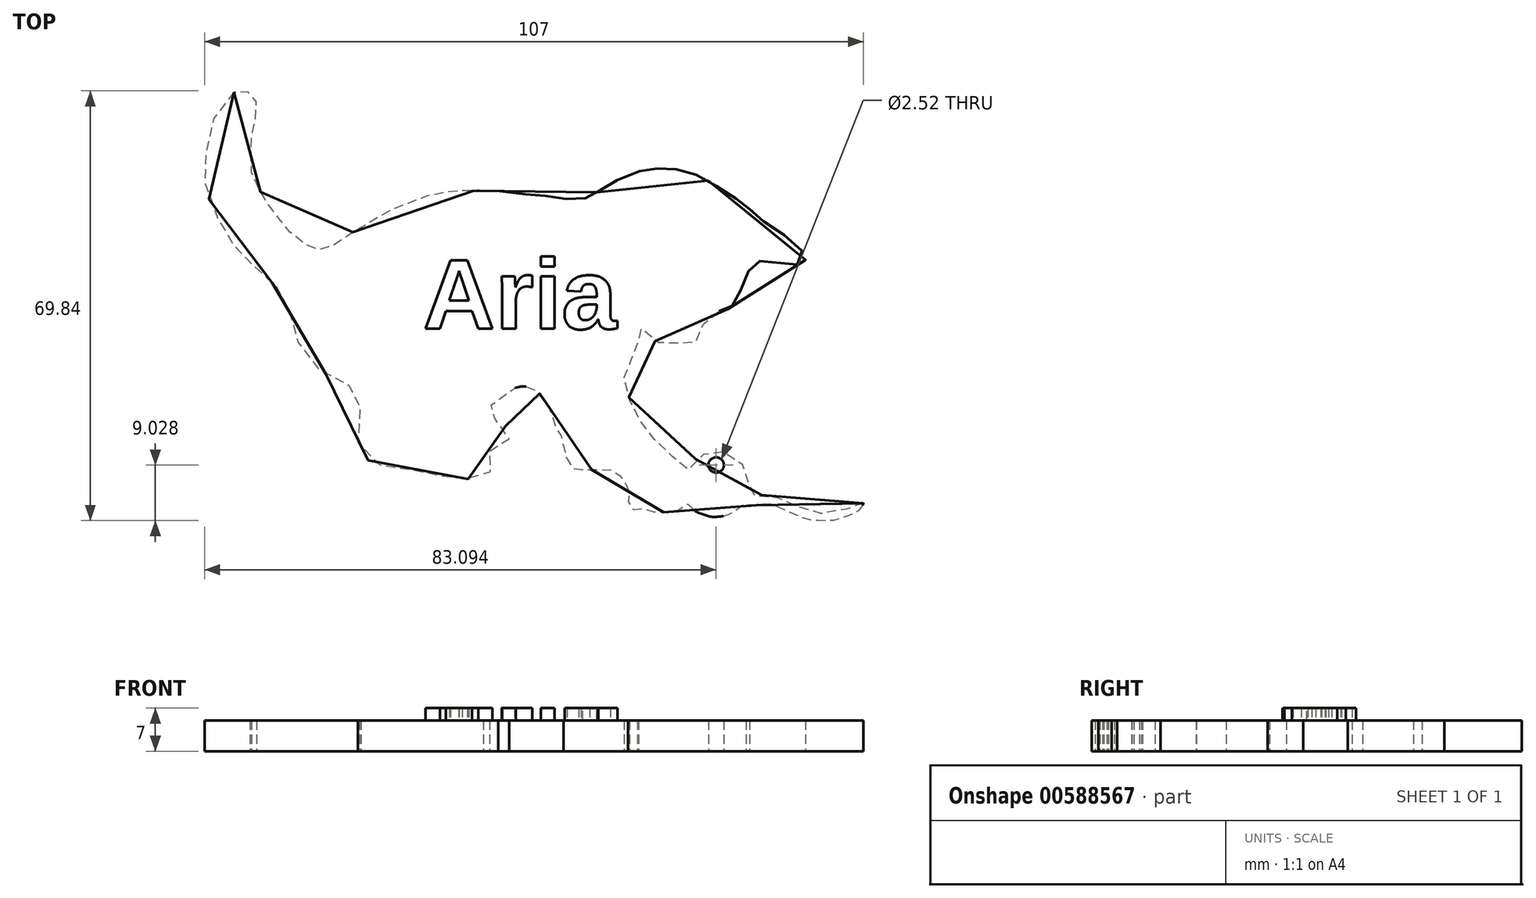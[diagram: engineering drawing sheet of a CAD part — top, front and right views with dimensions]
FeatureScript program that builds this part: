
annotation { "Feature Type Name" : "Feature", "Feature Type Description" : "" }
export const myFeature = defineFeature(function(context is Context, id is Id, definition is map)
    precondition{}
    {
        {
            var Q0;
            Q0=qCreatedBy(makeId("Top.planeOp"),FACE);
            var sketch = newSketch(context, id + "F0", { "sketchPlane" : qUnion([Q0])});
            skFitSpline(sketch, "E0", {"points": [v(-50.05, 29.56) * mm, v(-51.28, 28.57) * mm, v(-52.27, 27.19) * mm, v(-53.3, 25.4) * mm, v(-53.8, 23.53) * mm, v(-54.35, 21.95) * mm, v(-54.64, 19.63) * mm, v(-54.74, 17.95) * mm, v(-54.8, 16.76) * mm, v(-54.84, 15.43) * mm, v(-54.4, 13.06) * mm, v(-53.65, 10.84) * mm, v(-52.76, 9.16) * mm, v(-52.07, 7.77) * mm, v(-51.18, 6.34) * mm, v(-50.4, 5.1) * mm, v(-49.65, 4.17) * mm, v(-48.91, 3.57) * mm, v(-47.97, 2.44) * mm, v(-46.79, 1.25) * mm, v(-45.65, 0) * mm, v(-44.61, -0.82) * mm, v(-43.48, -1.76) * mm, v(-42.44, -2.6) * mm, v(-41.85, -3.04) * mm, v(-41.4, -4.38) * mm, v(-41.06, -6.1) * mm, v(-40.61, -8.33) * mm, v(-40.27, -9.56) * mm, v(-39.63, -11.15) * mm, v(-38.74, -12.92) * mm, v(-37.5, -14.4) * mm, v(-36.27, -15.5) * mm, v(-34.69, -16.48) * mm, v(-32.86, -17.27) * mm, v(-31.23, -18.2) * mm, v(-30.14, -19) * mm, v(-29.5, -19.6) * mm, v(-29.6, -20.83) * mm, v(-29.6, -22.3) * mm, v(-29.8, -24.24) * mm, v(-29.9, -26.3) * mm, v(-29.85, -28.04) * mm, v(-29, -29.42) * mm, v(-27.87, -30.6) * mm, v(-25.7, -31.15) * mm, v(-23.77, -31.64) * mm, v(-21.15, -31.84) * mm, v(-19.67, -32.04) * mm, v(-18.04, -32) * mm, v(-17.4, -32.14) * mm, v(-16.76, -32.58) * mm, v(-15.82, -33.08) * mm, v(-14.48, -33.57) * mm, v(-13.45, -33.42) * mm, v(-12.85, -33.23) * mm, v(-11.77, -33.37) * mm, v(-10.93, -33.52) * mm, v(-9.7, -32.93) * mm, v(-8.6, -32.19) * mm, v(-7.72, -32.04) * mm, v(-7.17, -30.9) * mm, v(-7.86, -29.42) * mm, v(-8.56, -28.78) * mm, v(-8.5, -28.58) * mm, v(-7.77, -28.48) * mm, v(-6.23, -28.04) * mm, v(-5.5, -27.25) * mm, v(-5.44, -25.82) * mm, v(-5.79, -24.88) * mm, v(-6.68, -24.19) * mm, v(-7.62, -23.54) * mm, v(-8.36, -23.1) * mm, v(-9.5, -23.1) * mm, v(-9.5, -22.8) * mm, v(-8.85, -21.96) * mm, v(-7.72, -20.68) * mm, v(-6.58, -19.79) * mm, v(-5.25, -18.8) * mm, v(-4.4, -18.5) * mm, v(-3.07, -18.26) * mm, v(-1.89, -18.5) * mm, v(-0.6, -19.25) * mm, v(0, -20.28) * mm, v(0.78, -21.32) * mm, v(1.57, -22.65) * mm, v(1.87, -24.09) * mm, v(2.26, -25.12) * mm, v(2.7, -25.96) * mm, v(3.4, -26.75) * mm, v(3.45, -28.33) * mm, v(3.94, -30.01) * mm, v(4.98, -31.6) * mm, v(6.6, -31.84) * mm, v(8.14, -31.8) * mm, v(10.66, -31.84) * mm, v(11.85, -32) * mm, v(12.83, -33.13) * mm, v(13.48, -34.06) * mm, v(14.12, -34.7) * mm, v(13.97, -36.04) * mm, v(13.97, -37.08) * mm, v(14.36, -38.02) * mm, v(15.45, -38.31) * mm, v(16.49, -38.12) * mm, v(17.82, -38.56) * mm, v(19.55, -38.7) * mm, v(21.13, -38.51) * mm, v(22.71, -38.12) * mm, v(23.85, -37.37) * mm, v(24.64, -38.31) * mm, v(26.02, -39.05) * mm, v(27.4, -39.45) * mm, v(29.33, -39.35) * mm, v(30.71, -38.9) * mm, v(31.85, -38.02) * mm, v(32.57, -37.58) * mm, v(33.82, -37.44) * mm, v(34.8, -37.58) * mm, v(36.16, -37.34) * mm, v(37.54, -37.52) * mm, v(39.33, -38.33) * mm, v(40.9, -39) * mm, v(42.8, -39.78) * mm, v(45.07, -40) * mm, v(47.44, -39.99) * mm, v(49.68, -39.25) * mm, v(50.8, -38.8) * mm, v(51.96, -37.84) * mm, v(52.05, -36.83) * mm, v(51.16, -37.42) * mm, v(49.53, -38.16) * mm, v(47.36, -38.86) * mm, v(45.43, -38.96) * mm, v(43.8, -38.56) * mm, v(42.12, -38.07) * mm, v(40.4, -37.23) * mm, v(39.11, -36.63) * mm, v(37.83, -36.29) * mm, v(36.1, -36) * mm, v(34.91, -36) * mm, v(33.13, -36.34) * mm, v(33.53, -35.25) * mm, v(33.63, -33.97) * mm, v(33.33, -32.68) * mm, v(32.6, -31.1) * mm, v(31.65, -30.16) * mm, v(30.17, -29.13) * mm, v(28.56, -28.9) * mm, v(27.4, -28.98) * mm, v(26.27, -29.32) * mm, v(24.98, -30.06) * mm, v(23.8, -31.5) * mm, v(23.65, -31.8) * mm, v(22.76, -31.05) * mm, v(21.63, -30.11) * mm, v(20.54, -29.08) * mm, v(19.16, -27.84) * mm, v(17.82, -26.4) * mm, v(17.08, -25.37) * mm, v(15.94, -23.89) * mm, v(15.2, -22.36) * mm, v(14.36, -20.88) * mm, v(13.82, -19.05) * mm, v(13.43, -17.52) * mm, v(13.33, -16.23) * mm, v(13.62, -15.2) * mm, v(14.22, -14.26) * mm, v(15.15, -13.07) * mm, v(15.6, -11.79) * mm, v(15.6, -11.1) * mm, v(15.45, -9.37) * mm, v(15.6, -8.43) * mm, v(16.49, -9.22) * mm, v(17.38, -10.3) * mm, v(18.71, -11.05) * mm, v(19.95, -11.3) * mm, v(21.77, -11.24) * mm, v(22.51, -11.2) * mm, v(23.2, -11.34) * mm, v(24.4, -11.44) * mm, v(25.03, -10.85) * mm, v(25.68, -9.56) * mm, v(26.02, -8.58) * mm, v(26.32, -7.84) * mm, v(27.16, -6.95) * mm, v(28.44, -6.2) * mm, v(29.33, -5.76) * mm, v(30.07, -5.71) * mm, v(31.01, -4.97) * mm, v(31.8, -3.64) * mm, v(32.44, -2.1) * mm, v(33.28, 0) * mm, v(33.73, 0.9) * mm, v(34.62, 1.8) * mm, v(35.7, 2.2) * mm, v(36.94, 1.94) * mm, v(38.67, 1.85) * mm, v(40.35, 1.6) * mm, v(42.62, 1.9) * mm, v(42.42, 3.43) * mm, v(40.7, 5.25) * mm, v(38.27, 7.03) * mm, v(35.9, 8.56) * mm, v(34.52, 9.8) * mm, v(33.58, 10.59) * mm, v(32.64, 11.43) * mm, v(31.36, 12.37) * mm, v(29.28, 13.65) * mm, v(26.86, 15.23) * mm, v(24.84, 16.22) * mm, v(22.86, 16.76) * mm, v(20.98, 17.1) * mm, v(19.3, 17.16) * mm, v(17.67, 17.16) * mm, v(16.2, 16.86) * mm, v(14.66, 16.32) * mm, v(11.65, 14.99) * mm, v(10.17, 14.05) * mm, v(9.08, 13.4) * mm, v(7.8, 12.52) * mm, v(6.6, 12.27) * mm, v(4.68, 12.22) * mm, v(3, 12.27) * mm, v(0.73, 12.66) * mm, v(-0.9, 12.86) * mm, v(-2.97, 12.96) * mm, v(-6.09, 13.36) * mm, v(-9.2, 13.6) * mm, v(-11.42, 13.55) * mm, v(-13.35, 13.5) * mm, v(-15.17, 13.36) * mm, v(-17.8, 12.91) * mm, v(-20.31, 12.12) * mm, v(-22.04, 11.38) * mm, v(-24.51, 10.44) * mm, v(-26.49, 9.3) * mm, v(-28.86, 7.87) * mm, v(-30.64, 6.88) * mm, v(-32.31, 5.7) * mm, v(-33.9, 4.71) * mm, v(-35.67, 4.02) * mm, v(-36.86, 4.02) * mm, v(-38.44, 4.8) * mm, v(-40.32, 6.24) * mm, v(-42.14, 8.07) * mm, v(-43.18, 9.65) * mm, v(-44.86, 11.77) * mm, v(-45.8, 13.45) * mm, v(-46.69, 15.13) * mm, v(-47.48, 17.9) * mm, v(-47.23, 19.73) * mm, v(-47.23, 21.95) * mm, v(-46.74, 24.37) * mm, v(-46.44, 26.89) * mm, v(-46.54, 28.47) * mm, v(-47.33, 29.36) * mm, v(-48.62, 29.75) * mm, v(-50.05, 29.56) * mm]});
            skSolve(sketch);
        }
        {
            var Q0;
            Q0 = qSketchRegion(id + "F2", true);
            var Q1;
            Q1=makeQuery(id+"F0.imprint","IMPRINT",FACE,{"disambiguationData":[TD([[makeQuery(id+"F0.imprint","IMPRINT",EDGE,{"derivedFrom":sQuery(id+"F0.wireOp",EDGE,"E0")}),1.0]])]});
            extrude(context, id + "F1", {"entities" : qUnion([Q0, Q1]), "depth" : 5 * mm, "offsetDistance" : 25 * mm});
        }
        {
            var Q0;
            Q0=makeQuery(id+"F1.opExtrude","CAP_FACE",FACE,{"disambiguationData":[OSD([sQuery(id+"F0.wireOp",EDGE,"E0")])],"isStart":false});
            var sketch = newSketch(context, id + "F2", { "sketchPlane" : qUnion([Q0])});
            skText(sketch, "E1", { "text": "Aria", "fontName": "Arimo-Bold.ttf"});
            const initialGuessF2  = {"E1": [-0.01936, -0.0089, 1, 0, 0.01166]};
            skSetInitialGuess(sketch, initialGuessF2);
            skSolve(sketch);
        }
        {
            var Q0;
            Q0 = qSketchRegion(id + "F2", true);
            var Q1;
            Q1 = qSketchRegion(id + "F4", true);
            extrude(context, id + "F3", {"entities" : qUnion([Q0, Q1]), "operationType" : NewBodyOperationType.ADD, "depth" : 2 * mm, "offsetDistance" : 25 * mm});
        }
        {
            var Q0;
            Q0=qCreatedBy(makeId("Front.planeOp"),FACE);
            var sketch = newSketch(context, id + "F4", { "sketchPlane" : qUnion([Q0])});
            skSolve(sketch);
        }
        {
            var Q0;
            Q0=qCreatedBy(makeId("Top.planeOp"),FACE);
            var sketch = newSketch(context, id + "F5", { "sketchPlane" : qUnion([Q0])});
            skCircle(sketch, "E2", {"center": v(28.72, -33.28) * mm, "radius": 1.26 * mm});
            skSolve(sketch);
        }
        {
            var Q0;
            Q0=makeQuery(id+"F5.imprint","IMPRINT",FACE,{"disambiguationData":[TD([[makeQuery(id+"F5.imprint","IMPRINT",EDGE,{"derivedFrom":sQuery(id+"F5.wireOp",EDGE,"E2")}),1.0]])]});
            extrude(context, id + "F6", {"entities" : qUnion([Q0]), "operationType" : NewBodyOperationType.ADD, "depth" : 5 * mm, "offsetDistance" : 25 * mm});
        }
        {
            var Q0;
            Q0=qCreatedBy(makeId("Top.planeOp"),FACE);
            var sketch = newSketch(context, id + "F7", { "sketchPlane" : qUnion([Q0])});
            skCircle(sketch, "E3", {"center": v(28.24, -31.04) * mm, "radius": 1.26 * mm});
            skSolve(sketch);
        }
        {
            var Q0;
            Q0=makeQuery(id+"F7.imprint","IMPRINT",FACE,{"disambiguationData":[TD([[makeQuery(id+"F7.imprint","IMPRINT",EDGE,{"derivedFrom":sQuery(id+"F7.wireOp",EDGE,"E3")}),1.0]])]});
            extrude(context, id + "F8", {"entities" : qUnion([Q0]), "operationType" : NewBodyOperationType.REMOVE, "depth" : 5 * mm, "offsetDistance" : 25 * mm});
        }
    });
